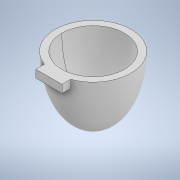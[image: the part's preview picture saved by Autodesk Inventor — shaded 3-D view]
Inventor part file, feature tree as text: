
AUTODESK INVENTOR PART (.ipt)
format: ipt  version: 2022 (Build 260153000, 153)  size: 250,368 bytes
history: native  units: in
note: dims shown in document units (in); Inventor stores cm internally (conversion verified against a paired STEP export)
features: sketch x2, revolve x1, shell x1, extrude x1
ambient origin geometry x8: Origin, YZ Plane, XZ Plane, XY Plane, X Axis, Y Axis, Z Axis, Center Point
bodies: Solid1 (feature_tree)
feature tree (5):
  revolve  "Revolution1"  [1 undecoded]
  shell  "Shell1"  Thickness=90.0deg
  extrude  "Extrusion1"  Depth=0.5in
  sketch  "Sketch1"  dims[d0=2.2in d1=1.2in d2=90.0deg]
  sketch  "Sketch2"  dims[d3=360.0deg d4=0.125in d7=0.5in d8=0.3in d10=0.15in d11=0.0in]
note: 1 required parameter value undecoded (feature->parameter linkage not recoverable at this tier; creation-order binding heuristic only, values carry confidence <= 0.55)
